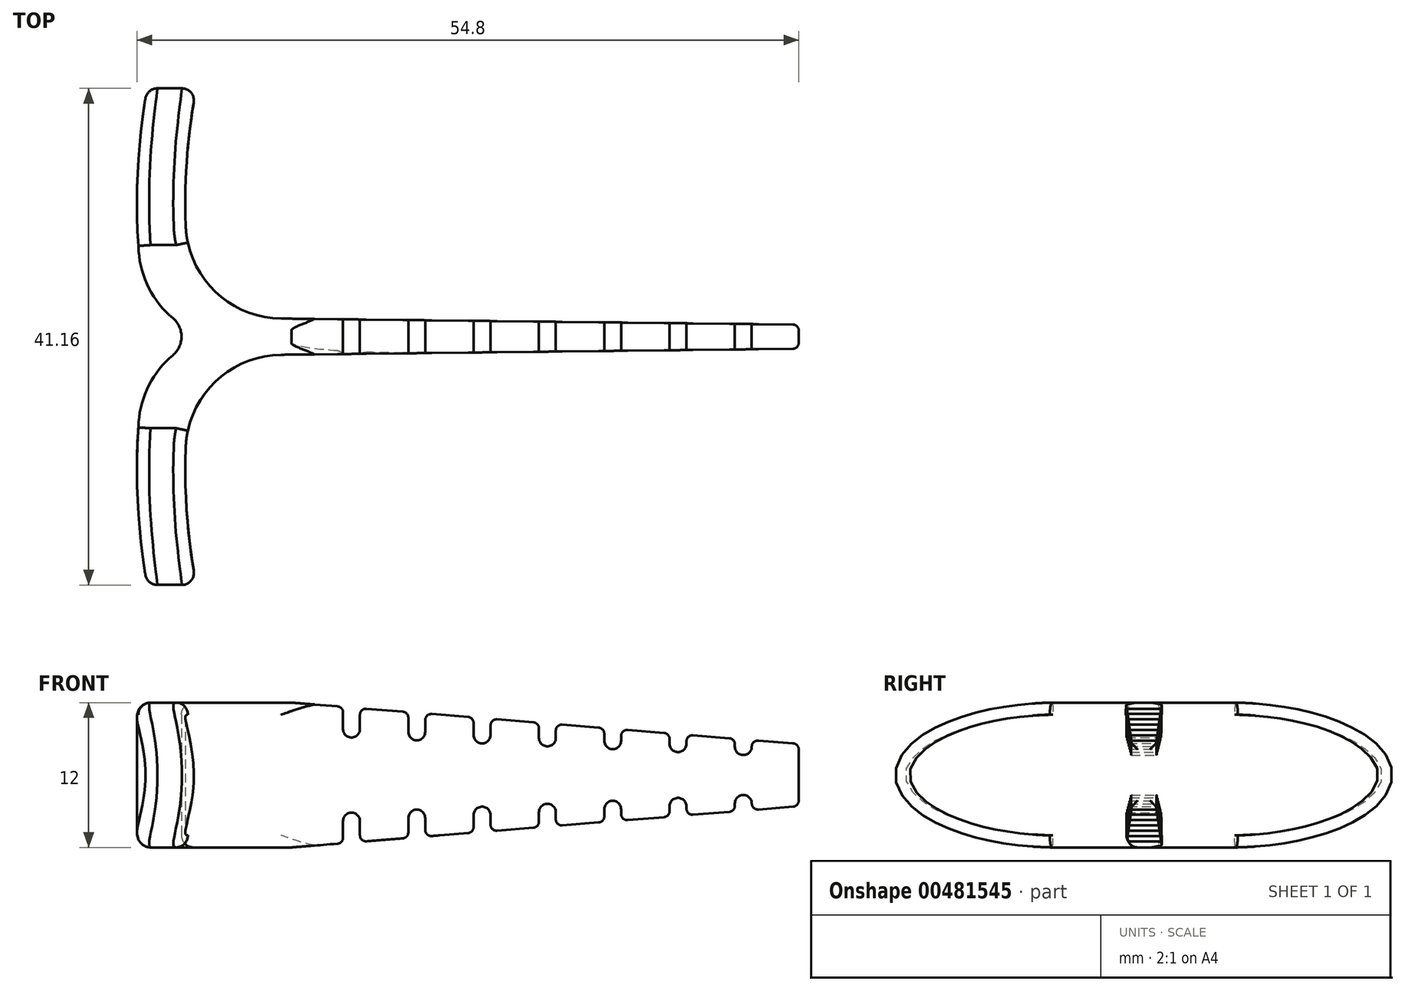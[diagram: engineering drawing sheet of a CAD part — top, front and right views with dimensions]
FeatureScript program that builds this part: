
annotation { "Feature Type Name" : "Feature", "Feature Type Description" : "" }
export const myFeature = defineFeature(function(context is Context, id is Id, definition is map)
    precondition{}
    {
        {
            var Q0;
            Q0=qCreatedBy(makeId("Top.planeOp"),FACE);
            var sketch = newSketch(context, id + "F0", { "sketchPlane" : qUnion([Q0])});
            skLineSegment(sketch, "E0.left", {"start": v(0, 0) * mm, "end": v(0, 2.01) * mm});
            skLineSegment(sketch, "E0.right", {"start": v(50, 0) * mm, "end": v(50, 1) * mm});
            skArc(sketch, "E1", {"start": v(-0.77, 9.22) * mm, "mid": v(-0.67, 14.63) * mm, "end": v(0, 20) * mm});
            skLineSegment(sketch, "E2", {"start": v(50, 11) * mm, "end": v(-65.07, 11) * mm, "construction": true});
            skArc(sketch, "E3.0", {"start": v(-4.66, 7.08) * mm, "mid": v(-4.72, 13.97) * mm, "end": v(-3.92, 20.8) * mm});
            skPoint(sketch, "E4.visualSharp", {"position": v(0, 2.01) * mm});
            skArc(sketch, "E4.filletArc", {"start": v(-0.77, 9.22) * mm, "mid": v(1.63, 3.78) * mm, "end": v(7.13, 1.5) * mm});
            skArc(sketch, "E5.filletArc", {"start": v(-4.66, 7.08) * mm, "mid": v(-3.8, 4.02) * mm, "end": v(-1.83, 1.53) * mm});
            skLineSegment(sketch, "E6.MirrorCS", {"start": v(0, 0) * mm, "end": v(0, -2.01) * mm});
            skLineSegment(sketch, "E7.MirrorCS", {"start": v(50, 0) * mm, "end": v(50, -1) * mm});
            skPoint(sketch, "E8.MirrorP", {"position": v(0, -2.01) * mm});
            skArc(sketch, "E9.MirrorCS", {"start": v(-4.66, -7.08) * mm, "mid": v(-3.8, -4.02) * mm, "end": v(-1.83, -1.53) * mm});
            skArc(sketch, "E10.MirrorCS", {"start": v(-0.77, -9.22) * mm, "mid": v(1.63, -3.78) * mm, "end": v(7.13, -1.5) * mm});
            skLineSegment(sketch, "E11", {"start": v(7.13, 1.5) * mm, "end": v(50, 1) * mm});
            skLineSegment(sketch, "E12", {"start": v(7.13, -1.5) * mm, "end": v(50, -1) * mm});
            skPoint(sketch, "E13.orphan", {"position": v(50, 2) * mm});
            skPoint(sketch, "E14.orphan", {"position": v(50, -2) * mm});
            skPoint(sketch, "E15.visualSharp", {"position": v(0, 20) * mm});
            skPoint(sketch, "E16.visualSharp", {"position": v(0.99, 0) * mm});
            skArc(sketch, "E16.filletArc", {"start": v(-1.83, -1.53) * mm, "mid": v(-1.12, 0) * mm, "end": v(-1.83, 1.53) * mm});
            skLineSegment(sketch, "E17", {"start": v(0, 20) * mm, "end": v(0.02, 20.14) * mm});
            skArc(sketch, "E18", {"start": v(-3.92, 20.8) * mm, "mid": v(-1.62, 22.42) * mm, "end": v(0.02, 20.14) * mm});
            skArc(sketch, "E19.MirrorCS", {"start": v(-0.77, -9.22) * mm, "mid": v(-0.67, -14.63) * mm, "end": v(0, -20) * mm});
            skArc(sketch, "E20.MirrorCS", {"start": v(-3.92, -20.8) * mm, "mid": v(-1.62, -22.42) * mm, "end": v(0.02, -20.14) * mm});
            skArc(sketch, "E21.MirrorCS", {"start": v(-4.66, -7.08) * mm, "mid": v(-4.72, -13.97) * mm, "end": v(-3.92, -20.8) * mm});
            skLineSegment(sketch, "E22", {"start": v(0, -20) * mm, "end": v(0.02, -20.14) * mm});
            skSolve(sketch);
        }
        {
            var Q0;
            Q0 = qSketchRegion(id + "F0", true);
            extrude(context, id + "F1", {"entities" : qUnion([Q0]), "depth" : 12 * mm});
        }
        {
            var Q0;
            Q0=qCreatedBy(makeId("Right.planeOp"),FACE);
            var sketch = newSketch(context, id + "F2", { "sketchPlane" : qUnion([Q0])});
            skLineSegment(sketch, "E23", {"start": v(23.44, 12) * mm, "end": v(-24.84, 12) * mm, "construction": true});
            skLineSegment(sketch, "E24", {"start": v(33.37, 6) * mm, "end": v(-34.66, 6) * mm, "construction": true});
            skLineSegment(sketch, "E25", {"start": v(-21, 14.87) * mm, "end": v(-21, -4.3) * mm, "construction": true});
            skEllipticalArc(sketch, "E26", {});
            skEllipticalArc(sketch, "E27.MirrorC", {});
            skLineSegment(sketch, "E28", {"start": v(6.46, 0) * mm, "end": v(-7, 0) * mm});
            skPoint(sketch, "E28.startSnap0", {"position": v(7.02, 0) * mm});
            skPoint(sketch, "E29.end.orphan", {"position": v(-7.02, 12) * mm});
            skPoint(sketch, "E29.start.orphan", {"position": v(7.02, 12) * mm});
            skPoint(sketch, "E30.orphan", {"position": v(-7.02, 0) * mm});
            skLineSegment(sketch, "E31", {"start": v(6.45, 12) * mm, "end": v(-6.45, 12) * mm});
            skLineSegment(sketch, "E32.bottom", {"start": v(27.3, 16.5) * mm, "end": v(-26.98, 16.5) * mm});
            skLineSegment(sketch, "E32.top", {"start": v(27.3, -5.8) * mm, "end": v(-26.98, -5.8) * mm});
            skLineSegment(sketch, "E32.left", {"start": v(27.3, 16.5) * mm, "end": v(27.3, -5.8) * mm});
            skLineSegment(sketch, "E32.right", {"start": v(-26.98, 16.5) * mm, "end": v(-26.98, -5.8) * mm});
            const initialGuessF2  = {"E26": [-0.007017247829487099, 0.006, -1, 0, 0.013559933993376927, 0.006005314895498056, 4.670313749696638, 1.5716514321059845], "E27.MirrorC": [0.007017247829487099, 0.006, 1, 0, 0.013559933993376927, 0.006005314895498056, 4.671160171773611, 1.6128715574829482]};
            skSetInitialGuess(sketch, initialGuessF2);
            skSolve(sketch);
        }
        {
            var Q0;
            Q0 = qSketchRegion(id + "F2", true);
            extrude(context, id + "F3", {"entities" : qUnion([Q0]), "operationType" : NewBodyOperationType.REMOVE, "endBound" : BoundingType.THROUGH_ALL, "oppositeDirection" : true, "depth" : 25 * mm, "hasSecondDirection" : true, "secondDirectionOppositeDirection" : false, "secondDirectionDepth" : 25 * mm});
        }
        {
            var Q0;
            Q0=qCreatedBy(makeId("Front.planeOp"),FACE);
            var sketch = newSketch(context, id + "F4", { "sketchPlane" : qUnion([Q0])});
            skLineSegment(sketch, "E33", {"start": v(-10.73, 6) * mm, "end": v(62.19, 6) * mm, "construction": true});
            skLineSegment(sketch, "E34", {"start": v(51, 26.55) * mm, "end": v(51, -11.53) * mm, "construction": true});
            skLineSegment(sketch, "E35", {"start": v(8, 21.37) * mm, "end": v(8, 12) * mm, "construction": true});
            skLineSegment(sketch, "E36", {"start": v(6.9, 12) * mm, "end": v(55.85, 12) * mm, "construction": true});
            skLineSegment(sketch, "E37", {"start": v(8, 12) * mm, "end": v(51, 8.5) * mm});
            skLineSegment(sketch, "E38", {"start": v(8, 0) * mm, "end": v(51, 3.5) * mm});
            skLineSegment(sketch, "E39", {"start": v(51, 8.5) * mm, "end": v(51, 3.5) * mm});
            skLineSegment(sketch, "E40.bottom", {"start": v(8, 21.37) * mm, "end": v(67.54, 21.37) * mm});
            skLineSegment(sketch, "E40.top", {"start": v(8, -12.27) * mm, "end": v(67.54, -12.27) * mm});
            skLineSegment(sketch, "E40.left", {"start": v(8, 21.37) * mm, "end": v(8, 12) * mm});
            skLineSegment(sketch, "E40.right", {"start": v(67.54, 21.37) * mm, "end": v(67.54, -12.27) * mm});
            skLineSegment(sketch, "E41.trimOffspring", {"start": v(8, 0) * mm, "end": v(8, -9.13) * mm, "construction": true});
            skLineSegment(sketch, "E42.trimOffspring", {"start": v(8, 0) * mm, "end": v(8, -12.27) * mm});
            skSolve(sketch);
        }
        {
            var Q0;
            Q0 = qSketchRegion(id + "F4", true);
            extrude(context, id + "F5", {"entities" : qUnion([Q0]), "operationType" : NewBodyOperationType.REMOVE, "endBound" : BoundingType.THROUGH_ALL, "oppositeDirection" : true, "depth" : 25 * mm, "hasSecondDirection" : true, "secondDirectionBound" : BoundingType.THROUGH_ALL, "secondDirectionOppositeDirection" : false, "secondDirectionDepth" : 25 * mm});
        }
        {
            var Q0;
            Q0=makeQuery(id+"F3.boolean.opBoolean","INTERSECT",EDGE,{"disambiguationData":[OD(1.0)],"derivedFrom":[makeQuery(id+"F1.opExtrude","SWEPT_FACE",FACE,{"disambiguationData":[OSD([sQuery(id+"F0.wireOp",EDGE,"E1")])]}),makeQuery(id+"F3.opExtrude","SWEPT_FACE",FACE,{"disambiguationData":[OSD([sQuery(id+"F2.wireOp",EDGE,"E27.MirrorC")])]})]});
            var Q1;
            Q1=makeQuery(id+"F1.opExtrude","CAP_EDGE",EDGE,{"disambiguationData":[OSD([sQuery(id+"F0.wireOp",EDGE,"E5.filletArc")])],"isStart":false});
            var Q2;
            Q2=makeQuery(id+"F1.opExtrude","CAP_EDGE",EDGE,{"disambiguationData":[OSD([sQuery(id+"F0.wireOp",EDGE,"E16.filletArc")])],"isStart":true});
            var Q3;
            Q3=makeQuery(id+"F3.boolean.opBoolean","INTERSECT",EDGE,{"derivedFrom":[makeQuery(id+"F1.opExtrude","SWEPT_FACE",FACE,{"disambiguationData":[OSD([sQuery(id+"F0.wireOp",EDGE,"E3.0")])]}),makeQuery(id+"F3.opExtrude","SWEPT_FACE",FACE,{"disambiguationData":[OSD([sQuery(id+"F2.wireOp",EDGE,"E27.MirrorC")])]})]});
            var Q4;
            Q4=makeQuery(id+"F3.boolean.opBoolean","INTERSECT",EDGE,{"derivedFrom":[makeQuery(id+"F1.opExtrude","SWEPT_FACE",FACE,{"disambiguationData":[OSD([sQuery(id+"F0.wireOp",EDGE,"E21.MirrorCS")])]}),makeQuery(id+"F3.opExtrude","SWEPT_FACE",FACE,{"disambiguationData":[OSD([sQuery(id+"F2.wireOp",EDGE,"E26")])]})]});
            fillet(context, id + "F6", {"entities" : qUnion([Q0, Q1, Q2, Q3, Q4]), "radius" : 1 * mm, "tangentPropagation" : true, "allowEdgeOverflow" : false});
        }
        {
            var Q0;
            Q0=makeQuery(id+"F1.opExtrude","CAP_EDGE",EDGE,{"disambiguationData":[OSD([sQuery(id+"F0.wireOp",EDGE,"E10.MirrorCS")])],"isStart":true});
            var Q1;
            Q1=makeQuery(id+"F3.boolean.opBoolean","INTERSECT",EDGE,{"disambiguationData":[OD(0.0)],"derivedFrom":[makeQuery(id+"F1.opExtrude","SWEPT_FACE",FACE,{"disambiguationData":[OSD([sQuery(id+"F0.wireOp",EDGE,"E19.MirrorCS")])]}),makeQuery(id+"F3.opExtrude","SWEPT_FACE",FACE,{"disambiguationData":[OSD([sQuery(id+"F2.wireOp",EDGE,"E26")])]})]});
            fillet(context, id + "F7", {"entities" : qUnion([Q0, Q1]), "radius" : 1 * mm, "tangentPropagation" : true, "allowEdgeOverflow" : false});
        }
        {
            var Q0;
            Q0=qCreatedBy(makeId("Front.planeOp"),FACE);
            var sketch = newSketch(context, id + "F8", { "sketchPlane" : qUnion([Q0])});
            skLineSegment(sketch, "E43", {"start": v(-7.48, 6) * mm, "end": v(53.6, 6) * mm, "construction": true});
            skLineSegment(sketch, "E44", {"start": v(12.96, 15.9) * mm, "end": v(12.96, 8.34) * mm, "construction": true});
            skLineSegment(sketch, "E45", {"start": v(12.26, 15.72) * mm, "end": v(12.26, 9.8) * mm});
            skLineSegment(sketch, "E46", {"start": v(13.66, 15.72) * mm, "end": v(13.66, 9.8) * mm});
            skArc(sketch, "E47", {"start": v(12.26, 9.8) * mm, "mid": v(12.96, 9.1) * mm, "end": v(13.66, 9.8) * mm});
            skLineSegment(sketch, "E48.1.0.0", {"start": v(19.07, 15.47) * mm, "end": v(19.07, 9.57) * mm});
            skLineSegment(sketch, "E48.1.0.1", {"start": v(17.67, 15.47) * mm, "end": v(17.67, 9.57) * mm});
            skArc(sketch, "E48.1.0.2", {"start": v(17.67, 9.57) * mm, "mid": v(18.37, 8.87) * mm, "end": v(19.07, 9.57) * mm});
            skLineSegment(sketch, "E48.1.0.3", {"start": v(18.37, 15.66) * mm, "end": v(18.37, 8.1) * mm, "construction": true});
            skLineSegment(sketch, "E48.2.0.0", {"start": v(24.47, 15.23) * mm, "end": v(24.47, 9.32) * mm});
            skLineSegment(sketch, "E48.2.0.1", {"start": v(23.07, 15.23) * mm, "end": v(23.07, 9.32) * mm});
            skArc(sketch, "E48.2.0.2", {"start": v(23.07, 9.32) * mm, "mid": v(23.77, 8.62) * mm, "end": v(24.47, 9.32) * mm});
            skLineSegment(sketch, "E48.2.0.3", {"start": v(23.77, 15.41) * mm, "end": v(23.77, 7.85) * mm, "construction": true});
            skLineSegment(sketch, "E48.3.0.0", {"start": v(29.88, 14.99) * mm, "end": v(29.88, 9.08) * mm});
            skLineSegment(sketch, "E48.3.0.1", {"start": v(28.48, 14.99) * mm, "end": v(28.48, 9.08) * mm});
            skArc(sketch, "E48.3.0.2", {"start": v(28.48, 9.08) * mm, "mid": v(29.18, 8.38) * mm, "end": v(29.88, 9.08) * mm});
            skLineSegment(sketch, "E48.3.0.3", {"start": v(29.18, 15.17) * mm, "end": v(29.18, 7.6) * mm, "construction": true});
            skLineSegment(sketch, "E48.4.0.0", {"start": v(35.3, 14.75) * mm, "end": v(35.3, 8.84) * mm});
            skLineSegment(sketch, "E48.4.0.1", {"start": v(33.9, 14.75) * mm, "end": v(33.9, 8.84) * mm});
            skArc(sketch, "E48.4.0.2", {"start": v(33.9, 8.84) * mm, "mid": v(34.6, 8.14) * mm, "end": v(35.3, 8.84) * mm});
            skLineSegment(sketch, "E48.4.0.3", {"start": v(34.6, 14.93) * mm, "end": v(34.6, 7.36) * mm, "construction": true});
            skLineSegment(sketch, "E48.5.0.0", {"start": v(40.7, 14.5) * mm, "end": v(40.7, 8.6) * mm});
            skLineSegment(sketch, "E48.5.0.1", {"start": v(39.3, 14.5) * mm, "end": v(39.3, 8.6) * mm});
            skArc(sketch, "E48.5.0.2", {"start": v(39.3, 8.6) * mm, "mid": v(40, 7.9) * mm, "end": v(40.7, 8.6) * mm});
            skLineSegment(sketch, "E48.5.0.3", {"start": v(40, 14.68) * mm, "end": v(40, 7.12) * mm, "construction": true});
            skLineSegment(sketch, "E48.6.0.0", {"start": v(46.1, 14.26) * mm, "end": v(46.1, 8.35) * mm});
            skLineSegment(sketch, "E48.6.0.1", {"start": v(44.7, 14.26) * mm, "end": v(44.7, 8.35) * mm});
            skArc(sketch, "E48.6.0.2", {"start": v(44.7, 8.35) * mm, "mid": v(45.4, 7.65) * mm, "end": v(46.1, 8.35) * mm});
            skLineSegment(sketch, "E48.6.0.3", {"start": v(45.4, 14.44) * mm, "end": v(45.4, 6.88) * mm, "construction": true});
            skLineSegment(sketch, "E48.direction1", {"start": v(12.96, 8.34) * mm, "end": v(18.37, 8.1) * mm, "construction": true});
            skArc(sketch, "E49.MirrorCS", {"start": v(12.26, 2.2) * mm, "mid": v(12.96, 2.9) * mm, "end": v(13.66, 2.2) * mm});
            skArc(sketch, "E50.MirrorCS", {"start": v(17.67, 2.43) * mm, "mid": v(18.37, 3.13) * mm, "end": v(19.07, 2.43) * mm});
            skArc(sketch, "E51.MirrorCS", {"start": v(28.48, 2.92) * mm, "mid": v(29.18, 3.62) * mm, "end": v(29.88, 2.92) * mm});
            skArc(sketch, "E52.MirrorCS", {"start": v(33.9, 3.16) * mm, "mid": v(34.6, 3.86) * mm, "end": v(35.3, 3.16) * mm});
            skArc(sketch, "E53.MirrorCS", {"start": v(23.07, 2.68) * mm, "mid": v(23.77, 3.38) * mm, "end": v(24.47, 2.68) * mm});
            skArc(sketch, "E54.MirrorCS", {"start": v(39.3, 3.4) * mm, "mid": v(40, 4.1) * mm, "end": v(40.7, 3.4) * mm});
            skArc(sketch, "E55.MirrorCS", {"start": v(44.7, 3.65) * mm, "mid": v(45.4, 4.35) * mm, "end": v(46.1, 3.65) * mm});
            skLineSegment(sketch, "E56.MirrorCS", {"start": v(35.3, -2.75) * mm, "end": v(35.3, 3.16) * mm});
            skLineSegment(sketch, "E57.MirrorCS", {"start": v(29.88, -2.99) * mm, "end": v(29.88, 2.92) * mm});
            skLineSegment(sketch, "E58.MirrorCS", {"start": v(28.48, -2.99) * mm, "end": v(28.48, 2.92) * mm});
            skLineSegment(sketch, "E59.MirrorCS", {"start": v(45.4, -2.44) * mm, "end": v(45.4, 5.12) * mm, "construction": true});
            skLineSegment(sketch, "E60.MirrorCS", {"start": v(44.7, -2.26) * mm, "end": v(44.7, 3.65) * mm});
            skLineSegment(sketch, "E61.MirrorCS", {"start": v(12.96, -3.9) * mm, "end": v(12.96, 3.66) * mm, "construction": true});
            skLineSegment(sketch, "E62.MirrorCS", {"start": v(12.26, -3.72) * mm, "end": v(12.26, 2.2) * mm});
            skLineSegment(sketch, "E63.MirrorCS", {"start": v(13.66, -3.72) * mm, "end": v(13.66, 2.2) * mm});
            skLineSegment(sketch, "E64.MirrorCS", {"start": v(19.07, -3.47) * mm, "end": v(19.07, 2.43) * mm});
            skLineSegment(sketch, "E65.MirrorCS", {"start": v(17.67, -3.47) * mm, "end": v(17.67, 2.43) * mm});
            skLineSegment(sketch, "E66.MirrorCS", {"start": v(40.7, -2.5) * mm, "end": v(40.7, 3.4) * mm});
            skLineSegment(sketch, "E67.MirrorCS", {"start": v(18.37, -3.66) * mm, "end": v(18.37, 3.9) * mm, "construction": true});
            skLineSegment(sketch, "E68.MirrorCS", {"start": v(24.47, -3.23) * mm, "end": v(24.47, 2.68) * mm});
            skLineSegment(sketch, "E69.MirrorCS", {"start": v(23.07, -3.23) * mm, "end": v(23.07, 2.68) * mm});
            skLineSegment(sketch, "E70.MirrorCS", {"start": v(23.77, -3.41) * mm, "end": v(23.77, 4.15) * mm, "construction": true});
            skLineSegment(sketch, "E71.MirrorCS", {"start": v(40, -2.68) * mm, "end": v(40, 4.88) * mm, "construction": true});
            skLineSegment(sketch, "E72.MirrorCS", {"start": v(33.9, -2.75) * mm, "end": v(33.9, 3.16) * mm});
            skLineSegment(sketch, "E73.MirrorCS", {"start": v(29.18, -3.17) * mm, "end": v(29.18, 4.4) * mm, "construction": true});
            skLineSegment(sketch, "E74.MirrorCS", {"start": v(12.96, 3.66) * mm, "end": v(18.37, 3.9) * mm, "construction": true});
            skLineSegment(sketch, "E75.MirrorCS", {"start": v(34.6, -2.93) * mm, "end": v(34.6, 4.64) * mm, "construction": true});
            skLineSegment(sketch, "E76.MirrorCS", {"start": v(46.1, -2.26) * mm, "end": v(46.1, 3.65) * mm});
            skLineSegment(sketch, "E77.MirrorCS", {"start": v(39.3, -2.5) * mm, "end": v(39.3, 3.4) * mm});
            skLineSegment(sketch, "E78", {"start": v(12.26, 15.72) * mm, "end": v(13.66, 15.72) * mm});
            skLineSegment(sketch, "E79", {"start": v(17.67, 15.47) * mm, "end": v(19.07, 15.47) * mm});
            skLineSegment(sketch, "E80", {"start": v(23.07, 15.23) * mm, "end": v(24.47, 15.23) * mm});
            skLineSegment(sketch, "E81", {"start": v(28.48, 14.99) * mm, "end": v(29.9, 14.99) * mm});
            skLineSegment(sketch, "E82", {"start": v(33.9, 14.75) * mm, "end": v(35.3, 14.75) * mm});
            skLineSegment(sketch, "E83", {"start": v(39.3, 14.5) * mm, "end": v(40.7, 14.5) * mm});
            skLineSegment(sketch, "E84", {"start": v(44.7, 14.26) * mm, "end": v(46.1, 14.26) * mm});
            skLineSegment(sketch, "E85", {"start": v(44.7, -2.26) * mm, "end": v(46.1, -2.26) * mm});
            skLineSegment(sketch, "E86", {"start": v(40.7, -2.5) * mm, "end": v(39.3, -2.5) * mm});
            skLineSegment(sketch, "E87", {"start": v(35.3, -2.75) * mm, "end": v(33.9, -2.75) * mm});
            skLineSegment(sketch, "E88", {"start": v(29.88, -2.99) * mm, "end": v(28.48, -2.99) * mm});
            skLineSegment(sketch, "E89", {"start": v(24.47, -3.23) * mm, "end": v(23.07, -3.23) * mm});
            skLineSegment(sketch, "E90", {"start": v(19.07, -3.47) * mm, "end": v(17.67, -3.47) * mm});
            skLineSegment(sketch, "E91", {"start": v(13.66, -3.72) * mm, "end": v(12.26, -3.72) * mm});
            skSolve(sketch);
        }
        {
            var Q0;
            Q0 = qSketchRegion(id + "F8", true);
            extrude(context, id + "F9", {"entities" : qUnion([Q0]), "operationType" : NewBodyOperationType.REMOVE, "endBound" : BoundingType.THROUGH_ALL, "depth" : 25 * mm, "hasSecondDirection" : true, "secondDirectionBound" : BoundingType.THROUGH_ALL, "secondDirectionOppositeDirection" : true, "secondDirectionDepth" : 25 * mm});
        }
        {
            var Q0;
            Q0=makeQuery(id+"F9.boolean.opBoolean","INTERSECT",EDGE,{"derivedFrom":[makeQuery(id+"F5.boolean.opBoolean","COPY",FACE,{"derivedFrom":makeQuery(id+"F5.opExtrude","SWEPT_FACE",FACE,{"disambiguationData":[OSD([sQuery(id+"F4.wireOp",EDGE,"E37")])]})}),makeQuery(id+"F9.opExtrude","SWEPT_FACE",FACE,{"disambiguationData":[OSD([sQuery(id+"F8.wireOp",EDGE,"E45")])]})]});
            var Q1;
            Q1=makeQuery(id+"F9.boolean.opBoolean","INTERSECT",EDGE,{"derivedFrom":[makeQuery(id+"F5.boolean.opBoolean","COPY",FACE,{"derivedFrom":makeQuery(id+"F5.opExtrude","SWEPT_FACE",FACE,{"disambiguationData":[OSD([sQuery(id+"F4.wireOp",EDGE,"E37")])]})}),makeQuery(id+"F9.opExtrude","SWEPT_FACE",FACE,{"disambiguationData":[OSD([sQuery(id+"F8.wireOp",EDGE,"E46")])]})]});
            var Q2;
            Q2=makeQuery(id+"F9.boolean.opBoolean","INTERSECT",EDGE,{"derivedFrom":[makeQuery(id+"F5.boolean.opBoolean","COPY",FACE,{"derivedFrom":makeQuery(id+"F5.opExtrude","SWEPT_FACE",FACE,{"disambiguationData":[OSD([sQuery(id+"F4.wireOp",EDGE,"E37")])]})}),makeQuery(id+"F9.opExtrude","SWEPT_FACE",FACE,{"disambiguationData":[OSD([sQuery(id+"F8.wireOp",EDGE,"E48.1.0.1")])]})]});
            var Q3;
            Q3=makeQuery(id+"F9.boolean.opBoolean","INTERSECT",EDGE,{"derivedFrom":[makeQuery(id+"F5.boolean.opBoolean","COPY",FACE,{"derivedFrom":makeQuery(id+"F5.opExtrude","SWEPT_FACE",FACE,{"disambiguationData":[OSD([sQuery(id+"F4.wireOp",EDGE,"E37")])]})}),makeQuery(id+"F9.opExtrude","SWEPT_FACE",FACE,{"disambiguationData":[OSD([sQuery(id+"F8.wireOp",EDGE,"E48.1.0.0")])]})]});
            var Q4;
            Q4=makeQuery(id+"F9.boolean.opBoolean","INTERSECT",EDGE,{"derivedFrom":[makeQuery(id+"F5.boolean.opBoolean","COPY",FACE,{"derivedFrom":makeQuery(id+"F5.opExtrude","SWEPT_FACE",FACE,{"disambiguationData":[OSD([sQuery(id+"F4.wireOp",EDGE,"E37")])]})}),makeQuery(id+"F9.opExtrude","SWEPT_FACE",FACE,{"disambiguationData":[OSD([sQuery(id+"F8.wireOp",EDGE,"E48.2.0.1")])]})]});
            var Q5;
            Q5=makeQuery(id+"F9.boolean.opBoolean","INTERSECT",EDGE,{"derivedFrom":[makeQuery(id+"F5.boolean.opBoolean","COPY",FACE,{"derivedFrom":makeQuery(id+"F5.opExtrude","SWEPT_FACE",FACE,{"disambiguationData":[OSD([sQuery(id+"F4.wireOp",EDGE,"E37")])]})}),makeQuery(id+"F9.opExtrude","SWEPT_FACE",FACE,{"disambiguationData":[OSD([sQuery(id+"F8.wireOp",EDGE,"E48.2.0.0")])]})]});
            var Q6;
            Q6=makeQuery(id+"F9.boolean.opBoolean","INTERSECT",EDGE,{"derivedFrom":[makeQuery(id+"F5.boolean.opBoolean","COPY",FACE,{"derivedFrom":makeQuery(id+"F5.opExtrude","SWEPT_FACE",FACE,{"disambiguationData":[OSD([sQuery(id+"F4.wireOp",EDGE,"E37")])]})}),makeQuery(id+"F9.opExtrude","SWEPT_FACE",FACE,{"disambiguationData":[OSD([sQuery(id+"F8.wireOp",EDGE,"E48.3.0.1")])]})]});
            var Q7;
            Q7=makeQuery(id+"F9.boolean.opBoolean","INTERSECT",EDGE,{"derivedFrom":[makeQuery(id+"F5.boolean.opBoolean","COPY",FACE,{"derivedFrom":makeQuery(id+"F5.opExtrude","SWEPT_FACE",FACE,{"disambiguationData":[OSD([sQuery(id+"F4.wireOp",EDGE,"E37")])]})}),makeQuery(id+"F9.opExtrude","SWEPT_FACE",FACE,{"disambiguationData":[OSD([sQuery(id+"F8.wireOp",EDGE,"E48.3.0.0")])]})]});
            var Q8;
            Q8=makeQuery(id+"F9.boolean.opBoolean","INTERSECT",EDGE,{"derivedFrom":[makeQuery(id+"F5.boolean.opBoolean","COPY",FACE,{"derivedFrom":makeQuery(id+"F5.opExtrude","SWEPT_FACE",FACE,{"disambiguationData":[OSD([sQuery(id+"F4.wireOp",EDGE,"E37")])]})}),makeQuery(id+"F9.opExtrude","SWEPT_FACE",FACE,{"disambiguationData":[OSD([sQuery(id+"F8.wireOp",EDGE,"E48.4.0.1")])]})]});
            var Q9;
            Q9=makeQuery(id+"F9.boolean.opBoolean","INTERSECT",EDGE,{"derivedFrom":[makeQuery(id+"F5.boolean.opBoolean","COPY",FACE,{"derivedFrom":makeQuery(id+"F5.opExtrude","SWEPT_FACE",FACE,{"disambiguationData":[OSD([sQuery(id+"F4.wireOp",EDGE,"E37")])]})}),makeQuery(id+"F9.opExtrude","SWEPT_FACE",FACE,{"disambiguationData":[OSD([sQuery(id+"F8.wireOp",EDGE,"E48.4.0.0")])]})]});
            var Q10;
            Q10=makeQuery(id+"F9.boolean.opBoolean","INTERSECT",EDGE,{"derivedFrom":[makeQuery(id+"F5.boolean.opBoolean","COPY",FACE,{"derivedFrom":makeQuery(id+"F5.opExtrude","SWEPT_FACE",FACE,{"disambiguationData":[OSD([sQuery(id+"F4.wireOp",EDGE,"E37")])]})}),makeQuery(id+"F9.opExtrude","SWEPT_FACE",FACE,{"disambiguationData":[OSD([sQuery(id+"F8.wireOp",EDGE,"E48.5.0.1")])]})]});
            var Q11;
            Q11=makeQuery(id+"F9.boolean.opBoolean","INTERSECT",EDGE,{"derivedFrom":[makeQuery(id+"F5.boolean.opBoolean","COPY",FACE,{"derivedFrom":makeQuery(id+"F5.opExtrude","SWEPT_FACE",FACE,{"disambiguationData":[OSD([sQuery(id+"F4.wireOp",EDGE,"E37")])]})}),makeQuery(id+"F9.opExtrude","SWEPT_FACE",FACE,{"disambiguationData":[OSD([sQuery(id+"F8.wireOp",EDGE,"E48.5.0.0")])]})]});
            var Q12;
            Q12=makeQuery(id+"F9.boolean.opBoolean","INTERSECT",EDGE,{"derivedFrom":[makeQuery(id+"F5.boolean.opBoolean","COPY",FACE,{"derivedFrom":makeQuery(id+"F5.opExtrude","SWEPT_FACE",FACE,{"disambiguationData":[OSD([sQuery(id+"F4.wireOp",EDGE,"E37")])]})}),makeQuery(id+"F9.opExtrude","SWEPT_FACE",FACE,{"disambiguationData":[OSD([sQuery(id+"F8.wireOp",EDGE,"E48.6.0.1")])]})]});
            var Q13;
            Q13=makeQuery(id+"F9.boolean.opBoolean","INTERSECT",EDGE,{"derivedFrom":[makeQuery(id+"F5.boolean.opBoolean","COPY",FACE,{"derivedFrom":makeQuery(id+"F5.opExtrude","SWEPT_FACE",FACE,{"disambiguationData":[OSD([sQuery(id+"F4.wireOp",EDGE,"E37")])]})}),makeQuery(id+"F9.opExtrude","SWEPT_FACE",FACE,{"disambiguationData":[OSD([sQuery(id+"F8.wireOp",EDGE,"E48.6.0.0")])]})]});
            var Q14;
            Q14=makeQuery(id+"F9.boolean.opBoolean","INTERSECT",EDGE,{"derivedFrom":[makeQuery(id+"F5.boolean.opBoolean","COPY",FACE,{"derivedFrom":makeQuery(id+"F5.opExtrude","SWEPT_FACE",FACE,{"disambiguationData":[OSD([sQuery(id+"F4.wireOp",EDGE,"E38")])]})}),makeQuery(id+"F9.opExtrude","SWEPT_FACE",FACE,{"disambiguationData":[OSD([sQuery(id+"F8.wireOp",EDGE,"E76.MirrorCS")])]})]});
            var Q15;
            Q15=makeQuery(id+"F9.boolean.opBoolean","INTERSECT",EDGE,{"derivedFrom":[makeQuery(id+"F5.boolean.opBoolean","COPY",FACE,{"derivedFrom":makeQuery(id+"F5.opExtrude","SWEPT_FACE",FACE,{"disambiguationData":[OSD([sQuery(id+"F4.wireOp",EDGE,"E38")])]})}),makeQuery(id+"F9.opExtrude","SWEPT_FACE",FACE,{"disambiguationData":[OSD([sQuery(id+"F8.wireOp",EDGE,"E60.MirrorCS")])]})]});
            var Q16;
            Q16=makeQuery(id+"F9.boolean.opBoolean","INTERSECT",EDGE,{"derivedFrom":[makeQuery(id+"F5.boolean.opBoolean","COPY",FACE,{"derivedFrom":makeQuery(id+"F5.opExtrude","SWEPT_FACE",FACE,{"disambiguationData":[OSD([sQuery(id+"F4.wireOp",EDGE,"E38")])]})}),makeQuery(id+"F9.opExtrude","SWEPT_FACE",FACE,{"disambiguationData":[OSD([sQuery(id+"F8.wireOp",EDGE,"E66.MirrorCS")])]})]});
            var Q17;
            Q17=makeQuery(id+"F9.boolean.opBoolean","INTERSECT",EDGE,{"derivedFrom":[makeQuery(id+"F5.boolean.opBoolean","COPY",FACE,{"derivedFrom":makeQuery(id+"F5.opExtrude","SWEPT_FACE",FACE,{"disambiguationData":[OSD([sQuery(id+"F4.wireOp",EDGE,"E38")])]})}),makeQuery(id+"F9.opExtrude","SWEPT_FACE",FACE,{"disambiguationData":[OSD([sQuery(id+"F8.wireOp",EDGE,"E77.MirrorCS")])]})]});
            var Q18;
            Q18=makeQuery(id+"F9.boolean.opBoolean","INTERSECT",EDGE,{"derivedFrom":[makeQuery(id+"F5.boolean.opBoolean","COPY",FACE,{"derivedFrom":makeQuery(id+"F5.opExtrude","SWEPT_FACE",FACE,{"disambiguationData":[OSD([sQuery(id+"F4.wireOp",EDGE,"E38")])]})}),makeQuery(id+"F9.opExtrude","SWEPT_FACE",FACE,{"disambiguationData":[OSD([sQuery(id+"F8.wireOp",EDGE,"E56.MirrorCS")])]})]});
            var Q19;
            Q19=makeQuery(id+"F9.boolean.opBoolean","INTERSECT",EDGE,{"derivedFrom":[makeQuery(id+"F5.boolean.opBoolean","COPY",FACE,{"derivedFrom":makeQuery(id+"F5.opExtrude","SWEPT_FACE",FACE,{"disambiguationData":[OSD([sQuery(id+"F4.wireOp",EDGE,"E38")])]})}),makeQuery(id+"F9.opExtrude","SWEPT_FACE",FACE,{"disambiguationData":[OSD([sQuery(id+"F8.wireOp",EDGE,"E72.MirrorCS")])]})]});
            var Q20;
            Q20=makeQuery(id+"F9.boolean.opBoolean","INTERSECT",EDGE,{"derivedFrom":[makeQuery(id+"F5.boolean.opBoolean","COPY",FACE,{"derivedFrom":makeQuery(id+"F5.opExtrude","SWEPT_FACE",FACE,{"disambiguationData":[OSD([sQuery(id+"F4.wireOp",EDGE,"E38")])]})}),makeQuery(id+"F9.opExtrude","SWEPT_FACE",FACE,{"disambiguationData":[OSD([sQuery(id+"F8.wireOp",EDGE,"E57.MirrorCS")])]})]});
            var Q21;
            Q21=makeQuery(id+"F9.boolean.opBoolean","INTERSECT",EDGE,{"derivedFrom":[makeQuery(id+"F5.boolean.opBoolean","COPY",FACE,{"derivedFrom":makeQuery(id+"F5.opExtrude","SWEPT_FACE",FACE,{"disambiguationData":[OSD([sQuery(id+"F4.wireOp",EDGE,"E38")])]})}),makeQuery(id+"F9.opExtrude","SWEPT_FACE",FACE,{"disambiguationData":[OSD([sQuery(id+"F8.wireOp",EDGE,"E58.MirrorCS")])]})]});
            var Q22;
            Q22=makeQuery(id+"F9.boolean.opBoolean","INTERSECT",EDGE,{"derivedFrom":[makeQuery(id+"F5.boolean.opBoolean","COPY",FACE,{"derivedFrom":makeQuery(id+"F5.opExtrude","SWEPT_FACE",FACE,{"disambiguationData":[OSD([sQuery(id+"F4.wireOp",EDGE,"E38")])]})}),makeQuery(id+"F9.opExtrude","SWEPT_FACE",FACE,{"disambiguationData":[OSD([sQuery(id+"F8.wireOp",EDGE,"E68.MirrorCS")])]})]});
            var Q23;
            Q23=makeQuery(id+"F9.boolean.opBoolean","INTERSECT",EDGE,{"derivedFrom":[makeQuery(id+"F5.boolean.opBoolean","COPY",FACE,{"derivedFrom":makeQuery(id+"F5.opExtrude","SWEPT_FACE",FACE,{"disambiguationData":[OSD([sQuery(id+"F4.wireOp",EDGE,"E38")])]})}),makeQuery(id+"F9.opExtrude","SWEPT_FACE",FACE,{"disambiguationData":[OSD([sQuery(id+"F8.wireOp",EDGE,"E69.MirrorCS")])]})]});
            var Q24;
            Q24=makeQuery(id+"F9.boolean.opBoolean","INTERSECT",EDGE,{"derivedFrom":[makeQuery(id+"F5.boolean.opBoolean","COPY",FACE,{"derivedFrom":makeQuery(id+"F5.opExtrude","SWEPT_FACE",FACE,{"disambiguationData":[OSD([sQuery(id+"F4.wireOp",EDGE,"E38")])]})}),makeQuery(id+"F9.opExtrude","SWEPT_FACE",FACE,{"disambiguationData":[OSD([sQuery(id+"F8.wireOp",EDGE,"E64.MirrorCS")])]})]});
            var Q25;
            Q25=makeQuery(id+"F9.boolean.opBoolean","INTERSECT",EDGE,{"derivedFrom":[makeQuery(id+"F5.boolean.opBoolean","COPY",FACE,{"derivedFrom":makeQuery(id+"F5.opExtrude","SWEPT_FACE",FACE,{"disambiguationData":[OSD([sQuery(id+"F4.wireOp",EDGE,"E38")])]})}),makeQuery(id+"F9.opExtrude","SWEPT_FACE",FACE,{"disambiguationData":[OSD([sQuery(id+"F8.wireOp",EDGE,"E65.MirrorCS")])]})]});
            var Q26;
            Q26=makeQuery(id+"F9.boolean.opBoolean","INTERSECT",EDGE,{"derivedFrom":[makeQuery(id+"F5.boolean.opBoolean","COPY",FACE,{"derivedFrom":makeQuery(id+"F5.opExtrude","SWEPT_FACE",FACE,{"disambiguationData":[OSD([sQuery(id+"F4.wireOp",EDGE,"E38")])]})}),makeQuery(id+"F9.opExtrude","SWEPT_FACE",FACE,{"disambiguationData":[OSD([sQuery(id+"F8.wireOp",EDGE,"E63.MirrorCS")])]})]});
            var Q27;
            Q27=makeQuery(id+"F9.boolean.opBoolean","INTERSECT",EDGE,{"derivedFrom":[makeQuery(id+"F5.boolean.opBoolean","COPY",FACE,{"derivedFrom":makeQuery(id+"F5.opExtrude","SWEPT_FACE",FACE,{"disambiguationData":[OSD([sQuery(id+"F4.wireOp",EDGE,"E38")])]})}),makeQuery(id+"F9.opExtrude","SWEPT_FACE",FACE,{"disambiguationData":[OSD([sQuery(id+"F8.wireOp",EDGE,"E62.MirrorCS")])]})]});
            fillet(context, id + "F10", {"entities" : qUnion([Q0, Q1, Q2, Q3, Q4, Q5, Q6, Q7, Q8, Q9, Q10, Q11, Q12, Q13, Q14, Q15, Q16, Q17, Q18, Q19, Q20, Q21, Q22, Q23, Q24, Q25, Q26, Q27]), "radius" : 0.5 * mm, "tangentPropagation" : true, "allowEdgeOverflow" : false});
        }
        {
            var Q0;
            Q0=makeQuery(id+"F1.opExtrude","SWEPT_EDGE",EDGE,{"disambiguationData":[OSD([sQuery(id+"F0.wireOp",EDGE,"E7.MirrorCS"),sQuery(id+"F0.wireOp",EDGE,"E12")])]});
            var Q1;
            Q1=makeQuery(id+"F5.boolean.opBoolean","INTERSECT",EDGE,{"derivedFrom":[makeQuery(id+"F1.opExtrude","SWEPT_FACE",FACE,{"disambiguationData":[OSD([sQuery(id+"F0.wireOp",EDGE,"E0.right"),sQuery(id+"F0.wireOp",EDGE,"E7.MirrorCS")])]}),makeQuery(id+"F5.opExtrude","SWEPT_FACE",FACE,{"disambiguationData":[OSD([sQuery(id+"F4.wireOp",EDGE,"E38")])]})]});
            var Q2;
            Q2=makeQuery(id+"F1.opExtrude","SWEPT_EDGE",EDGE,{"disambiguationData":[OSD([sQuery(id+"F0.wireOp",EDGE,"E0.right"),sQuery(id+"F0.wireOp",EDGE,"E11")])]});
            var Q3;
            Q3=makeQuery(id+"F1.opExtrude","SWEPT_FACE",FACE,{"disambiguationData":[OSD([sQuery(id+"F0.wireOp",EDGE,"E0.right"),sQuery(id+"F0.wireOp",EDGE,"E7.MirrorCS")])]});
            fillet(context, id + "F11", {"entities" : qUnion([Q0, Q1, Q2, Q3]), "radius" : 0.5 * mm, "tangentPropagation" : true, "allowEdgeOverflow" : false});
        }
    });
